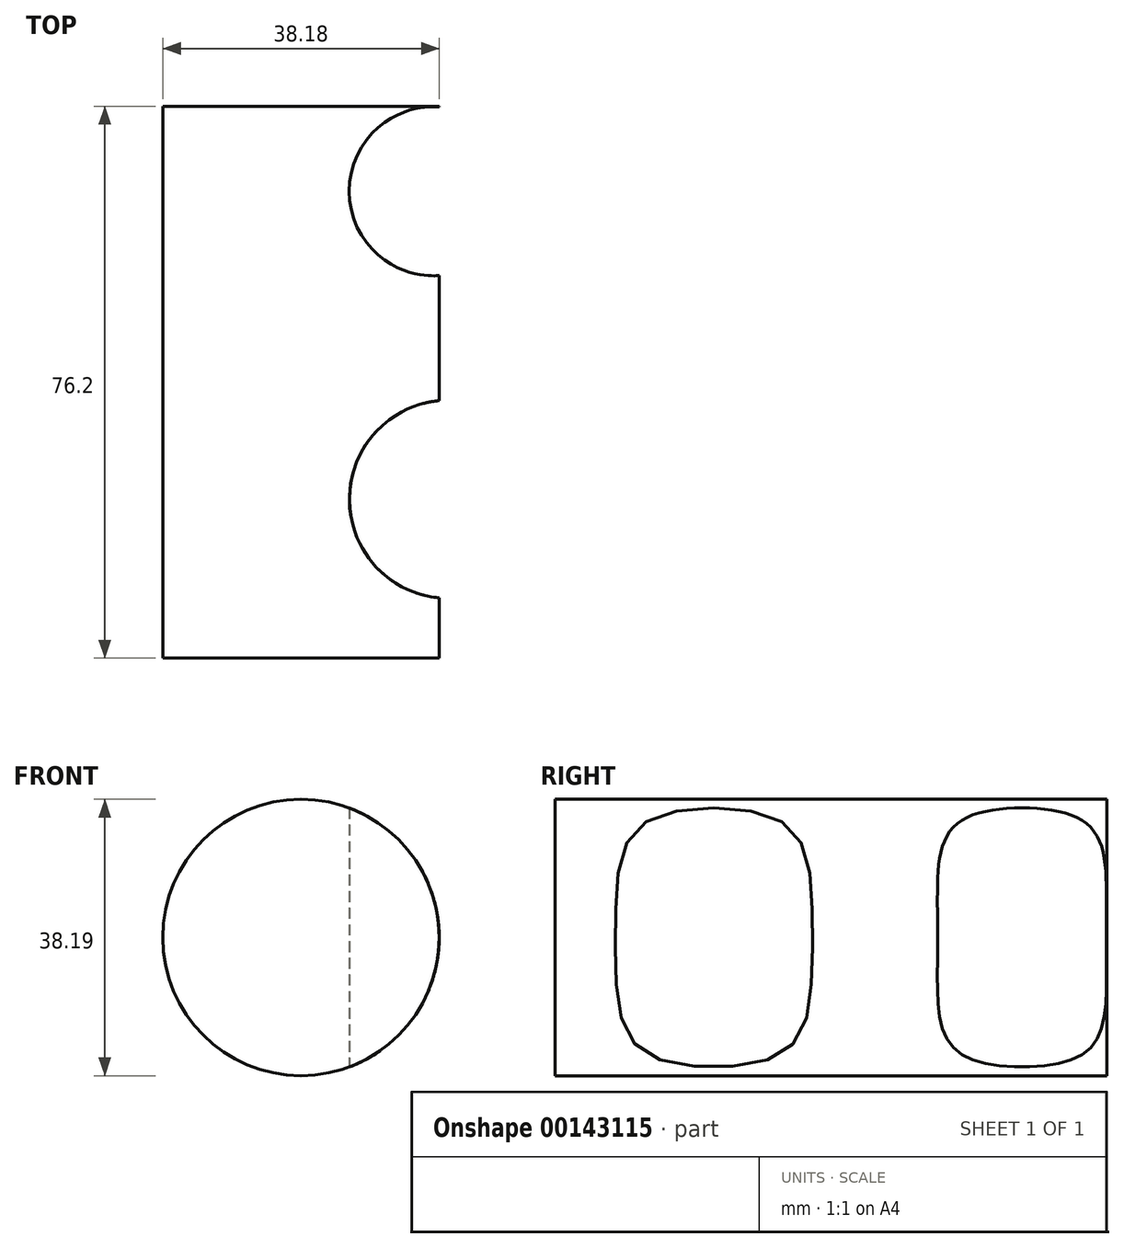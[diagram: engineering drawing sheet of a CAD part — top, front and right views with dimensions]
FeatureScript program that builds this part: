
annotation { "Feature Type Name" : "Feature", "Feature Type Description" : "" }
export const myFeature = defineFeature(function(context is Context, id is Id, definition is map)
    precondition{}
    {
        {
            var Q0;
            Q0=qCreatedBy(makeId("Front.planeOp"),FACE);
            var sketch = newSketch(context, id + "F0", { "sketchPlane" : qUnion([Q0])});
            skCircle(sketch, "E0", {"center": v(-42.91, 37.7) * mm, "radius": 19.1 * mm});
            skSolve(sketch);
        }
        {
            var Q0;
            Q0 = qSketchRegion(id + "F0", true);
            extrude(context, id + "F1", {"entities" : qUnion([Q0]), "endBound" : BoundingType.SYMMETRIC, "depth" : 76.2 * mm});
        }
        {
            var Q0;
            Q0=qCreatedBy(makeId("Top.planeOp"),FACE);
            var sketch = newSketch(context, id + "F2", { "sketchPlane" : qUnion([Q0])});
            skCircle(sketch, "E1", {"center": v(-24.57, 26.38) * mm, "radius": 11.68 * mm});
            skCircle(sketch, "E2", {"center": v(-22.53, -16.16) * mm, "radius": 13.68 * mm});
            skSolve(sketch);
        }
        {
            var Q0;
            Q0 = qSketchRegion(id + "F2", true);
            extrude(context, id + "F3", {"entities" : qUnion([Q0]), "operationType" : NewBodyOperationType.REMOVE, "endBound" : BoundingType.THROUGH_ALL, "depth" : 25.4 * mm});
        }
    });
